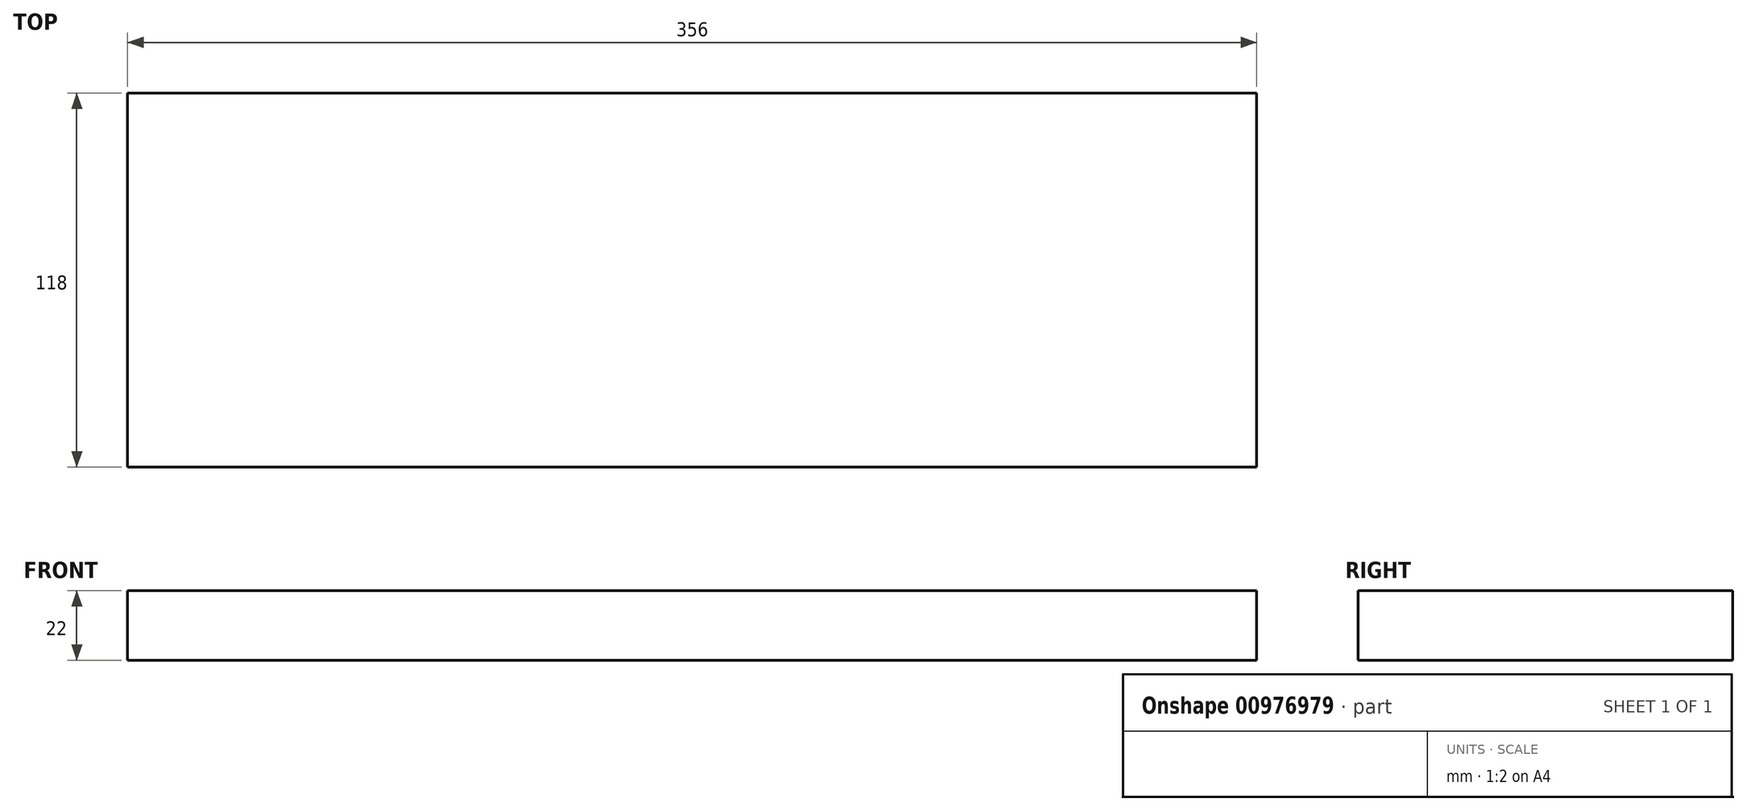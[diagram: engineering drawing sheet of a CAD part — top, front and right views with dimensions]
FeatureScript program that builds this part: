
annotation { "Feature Type Name" : "Feature", "Feature Type Description" : "" }
export const myFeature = defineFeature(function(context is Context, id is Id, definition is map)
    precondition{}
    {
        {
            var Q0;
            Q0=qCreatedBy(makeId("Top.planeOp"),FACE);
            var sketch = newSketch(context, id + "F0", { "sketchPlane" : qUnion([Q0])});
            skLineSegment(sketch, "E0.bottom", {"start": v(178, 59) * mm, "end": v(-178, 59) * mm});
            skLineSegment(sketch, "E0.top", {"start": v(178, -59) * mm, "end": v(-178, -59) * mm});
            skLineSegment(sketch, "E0.left", {"start": v(178, 59) * mm, "end": v(178, -59) * mm});
            skLineSegment(sketch, "E0.right", {"start": v(-178, 59) * mm, "end": v(-178, -59) * mm});
            skPoint(sketch, "E0.middle", {"position": v(0, 0) * mm});
            skSolve(sketch);
        }
        {
            var Q0;
            Q0 = qSketchRegion(id + "F0", true);
            extrude(context, id + "F1", {"entities" : qUnion([Q0]), "depth" : 22 * mm, "offsetDistance" : 25 * mm});
        }
    });
